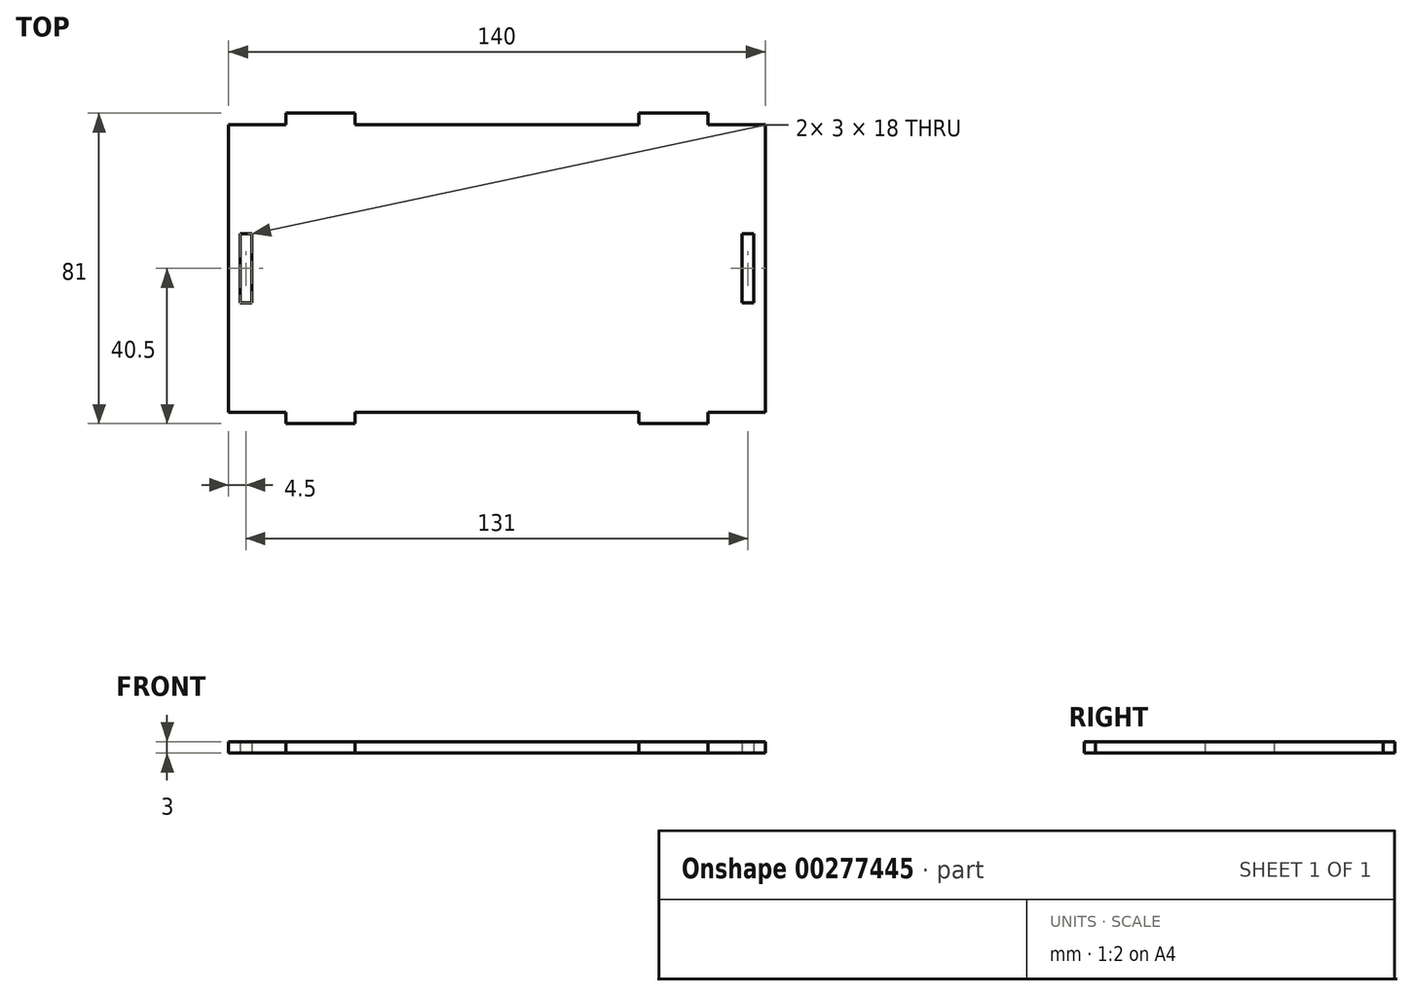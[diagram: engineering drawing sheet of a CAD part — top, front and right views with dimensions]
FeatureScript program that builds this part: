
annotation { "Feature Type Name" : "Feature", "Feature Type Description" : "" }
export const myFeature = defineFeature(function(context is Context, id is Id, definition is map)
    precondition{}
    {
        {
            var Q0;
            Q0=qCreatedBy(makeId("Top.planeOp"),FACE);
            var sketch = newSketch(context, id + "F0", { "sketchPlane" : qUnion([Q0])});
            skLineSegment(sketch, "E0.bottom", {"start": v(70, 37.5) * mm, "end": v(55, 37.5) * mm});
            skLineSegment(sketch, "E0.top", {"start": v(70, -37.5) * mm, "end": v(55, -37.5) * mm});
            skPoint(sketch, "E0.middle", {"position": v(0, 0) * mm});
            skLineSegment(sketch, "E1.top", {"start": v(-55, 40.5) * mm, "end": v(-37, 40.5) * mm});
            skLineSegment(sketch, "E1.left", {"start": v(-55, 37.5) * mm, "end": v(-55, 40.5) * mm});
            skLineSegment(sketch, "E1.right", {"start": v(-37, 37.5) * mm, "end": v(-37, 40.5) * mm});
            skLineSegment(sketch, "E2.top", {"start": v(37, 40.5) * mm, "end": v(55, 40.5) * mm});
            skLineSegment(sketch, "E2.left", {"start": v(37, 37.5) * mm, "end": v(37, 40.5) * mm});
            skLineSegment(sketch, "E2.right", {"start": v(55, 37.5) * mm, "end": v(55, 40.5) * mm});
            skLineSegment(sketch, "E3.top", {"start": v(37, -40.5) * mm, "end": v(55, -40.5) * mm});
            skLineSegment(sketch, "E3.left", {"start": v(37, -37.5) * mm, "end": v(37, -40.5) * mm});
            skLineSegment(sketch, "E3.right", {"start": v(55, -37.5) * mm, "end": v(55, -40.5) * mm});
            skLineSegment(sketch, "E4.top", {"start": v(-55, -40.5) * mm, "end": v(-37, -40.5) * mm});
            skLineSegment(sketch, "E4.left", {"start": v(-55, -37.5) * mm, "end": v(-55, -40.5) * mm});
            skLineSegment(sketch, "E4.right", {"start": v(-37, -37.5) * mm, "end": v(-37, -40.5) * mm});
            skLineSegment(sketch, "E5.trimOffspring", {"start": v(-55, 37.5) * mm, "end": v(-70, 37.5) * mm});
            skLineSegment(sketch, "E6.trimOffspring", {"start": v(37, 37.5) * mm, "end": v(-37, 37.5) * mm});
            skLineSegment(sketch, "E7.trimOffspring", {"start": v(37, -37.5) * mm, "end": v(-37, -37.5) * mm});
            skLineSegment(sketch, "E8.trimOffspring", {"start": v(-55, -37.5) * mm, "end": v(-70, -37.5) * mm});
            skLineSegment(sketch, "E9", {"start": v(0, 0) * mm, "end": v(0, 8.47) * mm, "construction": true});
            skLineSegment(sketch, "E10", {"start": v(0, 0) * mm, "end": v(7.23, 0) * mm, "construction": true});
            skLineSegment(sketch, "E11", {"start": v(-70, 37.5) * mm, "end": v(-70, -37.5) * mm});
            skLineSegment(sketch, "E12", {"start": v(70, 37.5) * mm, "end": v(70, -37.5) * mm});
            skLineSegment(sketch, "E13.bottom", {"start": v(-67, 9) * mm, "end": v(-64, 9) * mm});
            skLineSegment(sketch, "E13.top", {"start": v(-67, -9) * mm, "end": v(-64, -9) * mm});
            skLineSegment(sketch, "E13.left", {"start": v(-67, 9) * mm, "end": v(-67, -9) * mm});
            skLineSegment(sketch, "E13.right", {"start": v(-64, 9) * mm, "end": v(-64, -9) * mm});
            skLineSegment(sketch, "E14.bottom", {"start": v(64, 9) * mm, "end": v(67, 9) * mm});
            skLineSegment(sketch, "E14.top", {"start": v(64, -9) * mm, "end": v(67, -9) * mm});
            skLineSegment(sketch, "E14.left", {"start": v(64, 9) * mm, "end": v(64, -9) * mm});
            skLineSegment(sketch, "E14.right", {"start": v(67, 9) * mm, "end": v(67, -9) * mm});
            skSolve(sketch);
        }
        {
            var Q0;
            Q0=makeQuery(id+"F0.imprint","IMPRINT",FACE,{"disambiguationData":[TD([[makeQuery(id+"F0.imprint","IMPRINT",EDGE,{"derivedFrom":sQuery(id+"F0.wireOp",EDGE,"E0.bottom")}),1.0]])]});
            extrude(context, id + "F1", {"entities" : qUnion([Q0]), "depth" : 3 * mm});
        }
    });
